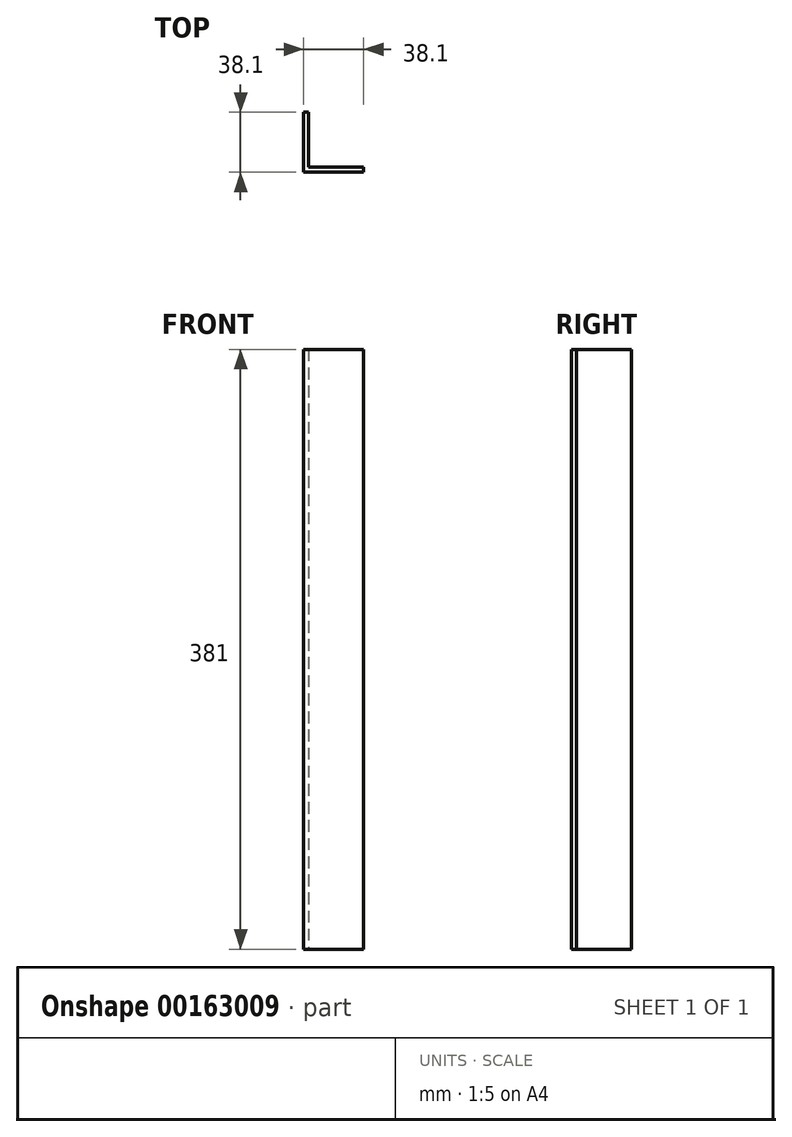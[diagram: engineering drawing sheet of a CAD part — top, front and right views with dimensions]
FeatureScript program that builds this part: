
annotation { "Feature Type Name" : "Feature", "Feature Type Description" : "" }
export const myFeature = defineFeature(function(context is Context, id is Id, definition is map)
    precondition{}
    {
        {
            var Q0;
            Q0=qCreatedBy(makeId("Top.planeOp"),FACE);
            var sketch = newSketch(context, id + "F0", { "sketchPlane" : qUnion([Q0])});
            skLineSegment(sketch, "E0", {"start": v(0, 38.1) * mm, "end": v(0, 0) * mm});
            skLineSegment(sketch, "E1", {"start": v(0, 0) * mm, "end": v(38.1, 0) * mm});
            skLineSegment(sketch, "E2.0", {"start": v(3.18, 3.18) * mm, "end": v(38.1, 3.18) * mm});
            skLineSegment(sketch, "E2.1", {"start": v(3.17, 38.1) * mm, "end": v(3.18, 3.18) * mm});
            skLineSegment(sketch, "E3", {"start": v(0, 38.1) * mm, "end": v(3.17, 38.1) * mm});
            skLineSegment(sketch, "E4", {"start": v(38.1, 3.18) * mm, "end": v(38.1, 0) * mm});
            skSolve(sketch);
        }
        {
            var Q0;
            Q0=qSketchRegion(id+"F0",true);
            extrude(context, id + "F1", {"entities" : qUnion([Q0]), "depth" : 381 * mm});
        }
    });
